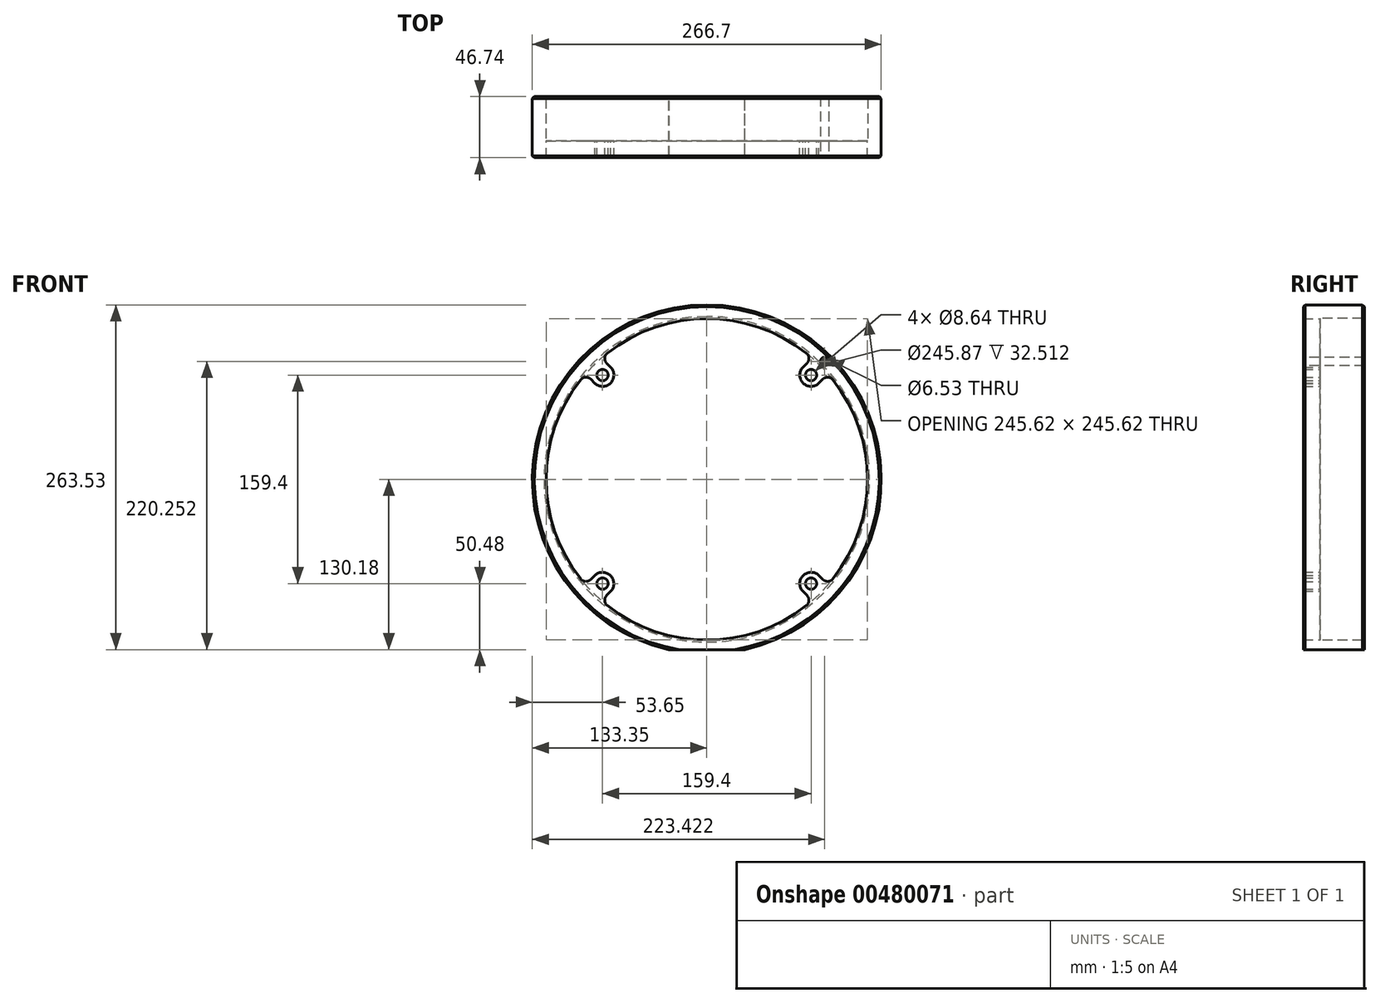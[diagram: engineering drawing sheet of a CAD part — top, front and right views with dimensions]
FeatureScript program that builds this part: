
annotation { "Feature Type Name" : "Feature", "Feature Type Description" : "" }
export const myFeature = defineFeature(function(context is Context, id is Id, definition is map)
    precondition{}
    {
        {
            var Q0;
            Q0=qCreatedBy(makeId("Front.planeOp"),FACE);
            var sketch = newSketch(context, id + "F0", { "sketchPlane" : qUnion([Q0])});
            skCircle(sketch, "E0", {"center": v(0, 0) * mm, "radius": 112.71 * mm, "construction": true});
            skLineSegment(sketch, "E1", {"start": v(0, 0) * mm, "end": v(100.3, 100.3) * mm, "construction": true});
            skCircle(sketch, "E2", {"center": v(79.7, 79.7) * mm, "radius": 4.32 * mm});
            skCircle(sketch, "E3.1.0", {"center": v(-79.7, 79.7) * mm, "radius": 4.32 * mm});
            skCircle(sketch, "E3.2.0", {"center": v(-79.7, -79.7) * mm, "radius": 4.32 * mm});
            skCircle(sketch, "E3.3.0", {"center": v(79.7, -79.7) * mm, "radius": 4.32 * mm});
            skArc(sketch, "E4", {"start": v(73.83, 86.03) * mm, "mid": v(73.57, 73.61) * mm, "end": v(86, 73.79) * mm});
            skArc(sketch, "E5", {"start": v(80.52, 92.73) * mm, "mid": v(0, 122.8) * mm, "end": v(-80.52, 92.73) * mm});
            skArc(sketch, "E6", {"start": v(28.93, -130.18) * mm, "mid": v(129.17, -33.12) * mm, "end": v(88, 100.2) * mm, "construction": true});
            skLineSegment(sketch, "E7", {"start": v(73.36, 85.57) * mm, "end": v(80.52, 92.73) * mm});
            skLineSegment(sketch, "E8", {"start": v(85.61, 73.4) * mm, "end": v(92.73, 80.52) * mm});
            skLineSegment(sketch, "E9.trimOffspring", {"start": v(88, 100.2) * mm, "end": v(88, 100.2) * mm});
            skLineSegment(sketch, "E10.trimOffspring", {"start": v(100.2, 88) * mm, "end": v(100.59, 88.38) * mm});
            skLineSegment(sketch, "E11.1.0", {"start": v(-85.57, 73.36) * mm, "end": v(-92.73, 80.52) * mm});
            skLineSegment(sketch, "E11.1.1", {"start": v(-73.4, 85.61) * mm, "end": v(-80.52, 92.73) * mm});
            skArc(sketch, "E11.1.2", {"start": v(-86.03, 73.83) * mm, "mid": v(-73.61, 73.57) * mm, "end": v(-73.79, 86) * mm});
            skLineSegment(sketch, "E11.2.0", {"start": v(-73.36, -85.57) * mm, "end": v(-80.52, -92.73) * mm});
            skLineSegment(sketch, "E11.2.1", {"start": v(-85.61, -73.4) * mm, "end": v(-92.73, -80.52) * mm});
            skArc(sketch, "E11.2.2", {"start": v(-73.83, -86.03) * mm, "mid": v(-73.57, -73.61) * mm, "end": v(-86, -73.79) * mm});
            skLineSegment(sketch, "E11.3.0", {"start": v(85.57, -73.36) * mm, "end": v(92.73, -80.52) * mm});
            skLineSegment(sketch, "E11.3.1", {"start": v(73.4, -85.61) * mm, "end": v(80.52, -92.73) * mm});
            skArc(sketch, "E11.3.2", {"start": v(86.03, -73.83) * mm, "mid": v(73.61, -73.57) * mm, "end": v(73.79, -86) * mm});
            skArc(sketch, "E12.trimOffspring", {"start": v(-92.73, 80.52) * mm, "mid": v(-122.8, 0) * mm, "end": v(-92.73, -80.52) * mm});
            skArc(sketch, "E13.trimOffspring", {"start": v(-80.52, -92.73) * mm, "mid": v(0, -122.8) * mm, "end": v(80.52, -92.73) * mm});
            skArc(sketch, "E14.trimOffspring", {"start": v(92.73, -80.52) * mm, "mid": v(122.8, 0) * mm, "end": v(92.73, 80.52) * mm});
            skLineSegment(sketch, "E15", {"start": v(-74.88, -130.18) * mm, "end": v(93, -130.18) * mm, "construction": true});
            skLineSegment(sketch, "E16", {"start": v(-28.93, -130.18) * mm, "end": v(28.93, -130.18) * mm});
            skArc(sketch, "E17.converted", {"start": v(28.93, -130.18) * mm, "mid": v(0, 133.35) * mm, "end": v(-28.93, -130.18) * mm});
            skSolve(sketch);
        }
        {
            var Q0;
            Q0=makeQuery(id+"F0.imprint","IMPRINT",FACE,{"disambiguationData":[TD([[makeQuery(id+"F0.imprint","IMPRINT",EDGE,{"derivedFrom":sQuery(id+"F0.wireOp",EDGE,"E2")}),-1.0]])]});
            extrude(context, id + "F1", {"entities" : qUnion([Q0]), "depth" : 12.7 * mm});
        }
        {
            var Q0;
            Q0=makeQuery(id+"F1.opExtrude","CAP_FACE",FACE,{"disambiguationData":[OSD([sQuery(id+"F0.wireOp",EDGE,"E2"),sQuery(id+"F0.wireOp",EDGE,"E3.1.0"),sQuery(id+"F0.wireOp",EDGE,"E3.2.0"),sQuery(id+"F0.wireOp",EDGE,"E3.3.0"),sQuery(id+"F0.wireOp",EDGE,"E4"),sQuery(id+"F0.wireOp",EDGE,"E5"),sQuery(id+"F0.wireOp",EDGE,"wtwuxn9d-5hRo-jlyd-y1oX-Cv7kF0Qcc7ff"),sQuery(id+"F0.wireOp",EDGE,"DTZbBTyo-910V-rojo-BSng-KiafCCvbkYSo"),sQuery(id+"F0.wireOp",EDGE,"GR1iSiWp-XWoq-ONjd-FFDE-OR4YaewtADHj"),sQuery(id+"F0.wireOp",EDGE,"E7"),sQuery(id+"F0.wireOp",EDGE,"E8"),sQuery(id+"F0.wireOp",EDGE,"E11.1.0"),sQuery(id+"F0.wireOp",EDGE,"E11.1.1"),sQuery(id+"F0.wireOp",EDGE,"E11.1.2"),sQuery(id+"F0.wireOp",EDGE,"E11.2.0"),sQuery(id+"F0.wireOp",EDGE,"E11.2.1"),sQuery(id+"F0.wireOp",EDGE,"E11.2.2"),sQuery(id+"F0.wireOp",EDGE,"E11.3.0"),sQuery(id+"F0.wireOp",EDGE,"E11.3.1"),sQuery(id+"F0.wireOp",EDGE,"E11.3.2"),sQuery(id+"F0.wireOp",EDGE,"E12.trimOffspring"),sQuery(id+"F0.wireOp",EDGE,"E13.trimOffspring"),sQuery(id+"F0.wireOp",EDGE,"E14.trimOffspring")])],"isStart":true});
            var sketch = newSketch(context, id + "F2", { "sketchPlane" : qUnion([Q0])});
            skCircle(sketch, "E18", {"center": v(0, 0) * mm, "radius": 136.93 * mm});
            skCircle(sketch, "E19", {"center": v(0, 0) * mm, "radius": 122.94 * mm});
            skSolve(sketch);
        }
        {
            var Q0;
            Q0=makeQuery(id+"F2.imprint","IMPRINT",FACE,{"disambiguationData":[TD([[makeQuery(id+"F2.imprint","IMPRINT",EDGE,{"derivedFrom":sQuery(id+"F2.wireOp",EDGE,"E19")}),-1.0]])]});
            extrude(context, id + "F3", {"entities" : qUnion([Q0]), "operationType" : NewBodyOperationType.ADD, "depth" : 34.04 * mm});
        }
        {
            var Q0;
            Q0=makeQuery(id+"F1.opExtrude","SWEPT_EDGE",EDGE,{"disambiguationData":[OSD([sQuery(id+"F0.wireOp",EDGE,"E5"),sQuery(id+"F0.wireOp",EDGE,"E11.1.1")])]});
            var Q1;
            Q1=makeQuery(id+"F1.opExtrude","SWEPT_EDGE",EDGE,{"disambiguationData":[OSD([sQuery(id+"F0.wireOp",EDGE,"E11.1.0"),sQuery(id+"F0.wireOp",EDGE,"E12.trimOffspring")])]});
            var Q2;
            Q2=makeQuery(id+"F1.opExtrude","SWEPT_EDGE",EDGE,{"disambiguationData":[OSD([sQuery(id+"F0.wireOp",EDGE,"E5"),sQuery(id+"F0.wireOp",EDGE,"E7")])]});
            var Q3;
            Q3=makeQuery(id+"F1.opExtrude","SWEPT_EDGE",EDGE,{"disambiguationData":[OSD([sQuery(id+"F0.wireOp",EDGE,"E8"),sQuery(id+"F0.wireOp",EDGE,"E14.trimOffspring")])]});
            var Q4;
            Q4=makeQuery(id+"F1.opExtrude","SWEPT_EDGE",EDGE,{"disambiguationData":[OSD([sQuery(id+"F0.wireOp",EDGE,"E11.3.0"),sQuery(id+"F0.wireOp",EDGE,"E14.trimOffspring")])]});
            var Q5;
            Q5=makeQuery(id+"F1.opExtrude","SWEPT_EDGE",EDGE,{"disambiguationData":[OSD([sQuery(id+"F0.wireOp",EDGE,"E11.3.1"),sQuery(id+"F0.wireOp",EDGE,"E13.trimOffspring")])]});
            var Q6;
            Q6=makeQuery(id+"F1.opExtrude","SWEPT_EDGE",EDGE,{"disambiguationData":[OSD([sQuery(id+"F0.wireOp",EDGE,"E11.2.0"),sQuery(id+"F0.wireOp",EDGE,"E13.trimOffspring")])]});
            var Q7;
            Q7=makeQuery(id+"F1.opExtrude","SWEPT_EDGE",EDGE,{"disambiguationData":[OSD([sQuery(id+"F0.wireOp",EDGE,"E11.2.1"),sQuery(id+"F0.wireOp",EDGE,"E12.trimOffspring")])]});
            fillet(context, id + "F4", {"entities" : qUnion([Q0, Q1, Q2, Q3, Q4, Q5, Q6, Q7]), "radius" : 5.08 * mm, "tangentPropagation" : true, "allowEdgeOverflow" : false});
        }
        {
            var Q0;
            Q0=makeQuery(id+"F1.opExtrude","CAP_FACE",FACE,{"disambiguationData":[OSD([sQuery(id+"F0.wireOp",EDGE,"E2"),sQuery(id+"F0.wireOp",EDGE,"E3.1.0"),sQuery(id+"F0.wireOp",EDGE,"E3.2.0"),sQuery(id+"F0.wireOp",EDGE,"E3.3.0"),sQuery(id+"F0.wireOp",EDGE,"E4"),sQuery(id+"F0.wireOp",EDGE,"E5"),sQuery(id+"F0.wireOp",EDGE,"E7"),sQuery(id+"F0.wireOp",EDGE,"E8"),sQuery(id+"F0.wireOp",EDGE,"E11.1.0"),sQuery(id+"F0.wireOp",EDGE,"E11.1.1"),sQuery(id+"F0.wireOp",EDGE,"E11.1.2"),sQuery(id+"F0.wireOp",EDGE,"E11.2.0"),sQuery(id+"F0.wireOp",EDGE,"E11.2.1"),sQuery(id+"F0.wireOp",EDGE,"E11.2.2"),sQuery(id+"F0.wireOp",EDGE,"E11.3.0"),sQuery(id+"F0.wireOp",EDGE,"E11.3.1"),sQuery(id+"F0.wireOp",EDGE,"E11.3.2"),sQuery(id+"F0.wireOp",EDGE,"E12.trimOffspring"),sQuery(id+"F0.wireOp",EDGE,"E13.trimOffspring"),sQuery(id+"F0.wireOp",EDGE,"E14.trimOffspring"),sQuery(id+"F0.wireOp",EDGE,"E16"),sQuery(id+"F0.wireOp",EDGE,"E17.converted")])],"isStart":false});
            var sketch = newSketch(context, id + "F5", { "sketchPlane" : qUnion([Q0])});
            skLineSegment(sketch, "E20", {"start": v(0, 0) * mm, "end": v(95.13, 95.13) * mm, "construction": true});
            skPoint(sketch, "E21.orphan", {"position": v(79.7, 79.7) * mm});
            skCircle(sketch, "E22", {"center": v(0, 0) * mm, "radius": 127.38 * mm, "construction": true});
            skPoint(sketch, "E23", {"position": v(90.07, 90.07) * mm});
            skSolve(sketch);
        }
        {
            var Q0;
            Q0=sQuery(id+"F5.wireOp",VERTEX,"E23");
            var Q1;
            Q1=makeQuery(id+"F1.opExtrude","SWEPT_BODY",BODY,{"disambiguationData":[OSD([sQuery(id+"F0.wireOp",EDGE,"E2"),sQuery(id+"F0.wireOp",EDGE,"E3.1.0"),sQuery(id+"F0.wireOp",EDGE,"E3.2.0"),sQuery(id+"F0.wireOp",EDGE,"E3.3.0"),sQuery(id+"F0.wireOp",EDGE,"E4"),sQuery(id+"F0.wireOp",EDGE,"E5"),sQuery(id+"F0.wireOp",EDGE,"wtwuxn9d-5hRo-jlyd-y1oX-Cv7kF0Qcc7ff"),sQuery(id+"F0.wireOp",EDGE,"DTZbBTyo-910V-rojo-BSng-KiafCCvbkYSo"),sQuery(id+"F0.wireOp",EDGE,"GR1iSiWp-XWoq-ONjd-FFDE-OR4YaewtADHj"),sQuery(id+"F0.wireOp",EDGE,"E7"),sQuery(id+"F0.wireOp",EDGE,"E8"),sQuery(id+"F0.wireOp",EDGE,"E11.1.0"),sQuery(id+"F0.wireOp",EDGE,"E11.1.1"),sQuery(id+"F0.wireOp",EDGE,"E11.1.2"),sQuery(id+"F0.wireOp",EDGE,"E11.2.0"),sQuery(id+"F0.wireOp",EDGE,"E11.2.1"),sQuery(id+"F0.wireOp",EDGE,"E11.2.2"),sQuery(id+"F0.wireOp",EDGE,"E11.3.0"),sQuery(id+"F0.wireOp",EDGE,"E11.3.1"),sQuery(id+"F0.wireOp",EDGE,"E11.3.2"),sQuery(id+"F0.wireOp",EDGE,"E12.trimOffspring"),sQuery(id+"F0.wireOp",EDGE,"E13.trimOffspring"),sQuery(id+"F0.wireOp",EDGE,"E14.trimOffspring")])]});
            hole(context, id + "F6", {"style" : HoleStyle.SIMPLE, "endStyle" : HoleEndStyle.THROUGH, "standardTappedOrClearance" : lookupTablePath({ "standard" : "ANSI", "engagement" : "75%", "pitch" : "18 tpi", "size" : "5/16", "type" : "Tapped" }), "standardBlindInLast" : lookupTablePath({ "standard" : "ANSI", "engagement" : "75%", "pitch" : "18 tpi", "size" : "5/16", "type" : "Tapped" }), "holeDiameter" : 6.53 * mm, "showTappedDepth" : true, "isTappedThrough" : true, "tappedDepth" : 12.7 * mm, "tapClearance" : 3, "locations" : qUnion([Q0]), "scope" : qUnion([Q1]), "majorDiameter" : 7.94 * mm});
        }
        {
            var Q0;
            {var subQ0=sQuery(id+"F0.wireOp",EDGE,"E17.converted");Q0=makeQuery(id+"F3.boolean.opBoolean","MERGE",FACE,{"derivedFrom":[makeQuery(id+"F1.opExtrude","SWEPT_FACE",FACE,{"disambiguationData":[OSD([subQ0])]}),makeQuery(id+"F3.opExtrude","SWEPT_FACE",FACE,{"disambiguationData":[OSD([subQ0])]})]});}
            var Q1;
            Q1=makeQuery(id+"F3.opExtrude","CAP_EDGE",EDGE,{"disambiguationData":[OSD([sQuery(id+"F2.wireOp",EDGE,"E19")])],"isStart":false});
            chamfer(context, id + "F7", {"entities" : qUnion([Q0, Q1]), "width" : 1.52 * mm, "tangentPropagation" : true});
        }
    });
